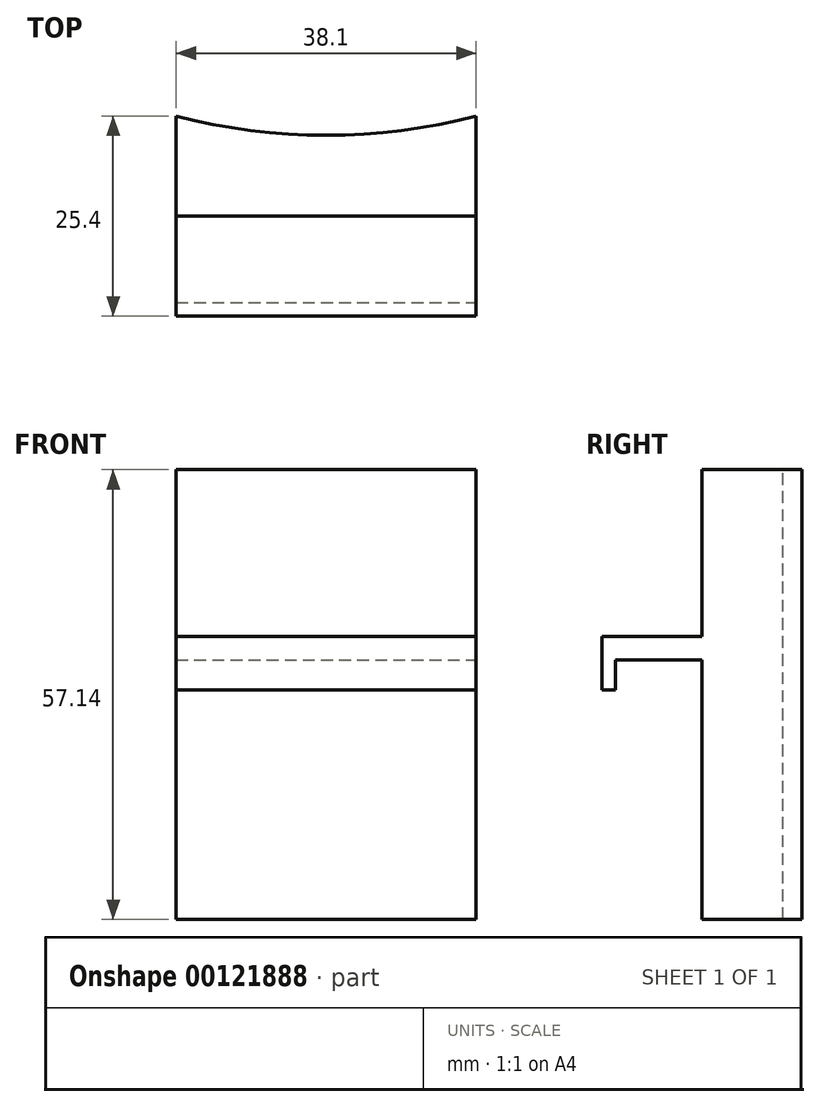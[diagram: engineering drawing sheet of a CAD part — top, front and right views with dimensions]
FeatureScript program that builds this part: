
annotation { "Feature Type Name" : "Feature", "Feature Type Description" : "" }
export const myFeature = defineFeature(function(context is Context, id is Id, definition is map)
    precondition{}
    {
        {
            var Q0;
            Q0=qCreatedBy(makeId("Front.planeOp"),FACE);
            var sketch = newSketch(context, id + "F0", { "sketchPlane" : qUnion([Q0])});
            skLineSegment(sketch, "E0.bottom", {"start": v(-19.05, 28.58) * mm, "end": v(19.05, 28.58) * mm});
            skLineSegment(sketch, "E0.top", {"start": v(-19.05, -28.57) * mm, "end": v(19.05, -28.57) * mm});
            skLineSegment(sketch, "E0.left", {"start": v(-19.05, 28.58) * mm, "end": v(-19.05, -28.57) * mm});
            skLineSegment(sketch, "E0.right", {"start": v(19.05, 28.58) * mm, "end": v(19.05, -28.57) * mm});
            skPoint(sketch, "E0.middle", {"position": v(0, 0) * mm});
            skSolve(sketch);
        }
        {
            var Q0;
            Q0=makeQuery(id+"F0.imprint","IMPRINT",FACE,{"disambiguationData":[TD([[makeQuery(id+"F0.imprint","IMPRINT",EDGE,{"derivedFrom":sQuery(id+"F0.wireOp",EDGE,"E0.bottom")}),-1.0]])]});
            extrude(context, id + "F1", {"entities" : qUnion([Q0]), "depth" : 12.7 * mm});
        }
        {
            var Q0;
            Q0=makeQuery(id+"F1.opExtrude","SWEPT_FACE",FACE,{"disambiguationData":[OSD([sQuery(id+"F0.wireOp",EDGE,"E0.bottom")])]});
            var sketch = newSketch(context, id + "F2", { "sketchPlane" : qUnion([Q0])});
            skArc(sketch, "E1", {"start": v(-19.05, 0) * mm, "mid": v(0, -2.42) * mm, "end": v(19.05, 0) * mm});
            skSolve(sketch);
        }
        {
            var Q0;
            Q0=makeQuery(id+"F2.imprint","IMPRINT",FACE,{"disambiguationData":[TD([[makeQuery(id+"F2.imprint","IMPRINT",EDGE,{"derivedFrom":sQuery(id+"F2.wireOp",EDGE,"E1")}),1.0]])]});
            extrude(context, id + "F3", {"entities" : qUnion([Q0]), "operationType" : NewBodyOperationType.REMOVE, "endBound" : BoundingType.THROUGH_ALL, "oppositeDirection" : true, "depth" : 25.4 * mm});
        }
        {
            var Q0;
            Q0=makeQuery(id+"F1.opExtrude","CAP_FACE",FACE,{"disambiguationData":[OSD([sQuery(id+"F0.wireOp",EDGE,"E0.bottom"),sQuery(id+"F0.wireOp",EDGE,"E0.top"),sQuery(id+"F0.wireOp",EDGE,"E0.left"),sQuery(id+"F0.wireOp",EDGE,"E0.right")])],"isStart":false});
            var sketch = newSketch(context, id + "F4", { "sketchPlane" : qUnion([Q0])});
            skLineSegment(sketch, "E2.bottom", {"start": v(-19.05, 7.35) * mm, "end": v(19.05, 7.35) * mm});
            skLineSegment(sketch, "E2.top", {"start": v(-19.05, 4.4) * mm, "end": v(19.05, 4.4) * mm});
            skLineSegment(sketch, "E2.left", {"start": v(-19.05, 7.35) * mm, "end": v(-19.05, 4.4) * mm});
            skLineSegment(sketch, "E2.right", {"start": v(19.05, 7.35) * mm, "end": v(19.05, 4.4) * mm});
            skLineSegment(sketch, "E3.bottom", {"start": v(-19.05, -3.4) * mm, "end": v(19.05, -3.4) * mm});
            skLineSegment(sketch, "E3.top", {"start": v(-19.05, -7.02) * mm, "end": v(19.05, -7.02) * mm});
            skLineSegment(sketch, "E3.left", {"start": v(-19.05, -3.4) * mm, "end": v(-19.05, -7.02) * mm});
            skLineSegment(sketch, "E3.right", {"start": v(19.05, -3.4) * mm, "end": v(19.05, -7.02) * mm});
            skSolve(sketch);
        }
        {
            var Q0;
            Q0=makeQuery(id+"F4.imprint","IMPRINT",FACE,{"disambiguationData":[TD([[makeQuery(id+"F4.imprint","IMPRINT",EDGE,{"derivedFrom":sQuery(id+"F4.wireOp",EDGE,"E2.bottom")}),-1.0]])]});
            extrude(context, id + "F5", {"entities" : qUnion([Q0]), "operationType" : NewBodyOperationType.ADD, "depth" : 12.7 * mm});
        }
        {
            var Q0;
            Q0=makeQuery(id+"F5.opExtrude","SWEPT_FACE",FACE,{"disambiguationData":[OSD([sQuery(id+"F4.wireOp",EDGE,"E2.top")])]});
            var sketch = newSketch(context, id + "F6", { "sketchPlane" : qUnion([Q0])});
            skLineSegment(sketch, "E4.bottom", {"start": v(-19.05, 25.4) * mm, "end": v(19.05, 25.4) * mm});
            skLineSegment(sketch, "E4.top", {"start": v(-19.05, 23.67) * mm, "end": v(19.05, 23.67) * mm});
            skLineSegment(sketch, "E4.left", {"start": v(-19.05, 25.4) * mm, "end": v(-19.05, 23.67) * mm});
            skLineSegment(sketch, "E4.right", {"start": v(19.05, 25.4) * mm, "end": v(19.05, 23.67) * mm});
            skSolve(sketch);
        }
        {
            var Q0;
            Q0=makeQuery(id+"F6.imprint","IMPRINT",FACE,{"disambiguationData":[TD([[makeQuery(id+"F6.imprint","IMPRINT",EDGE,{"derivedFrom":sQuery(id+"F6.wireOp",EDGE,"E4.bottom")}),-1.0]])]});
            extrude(context, id + "F7", {"entities" : qUnion([Q0]), "operationType" : NewBodyOperationType.ADD, "depth" : 3.8 * mm});
        }
    });
